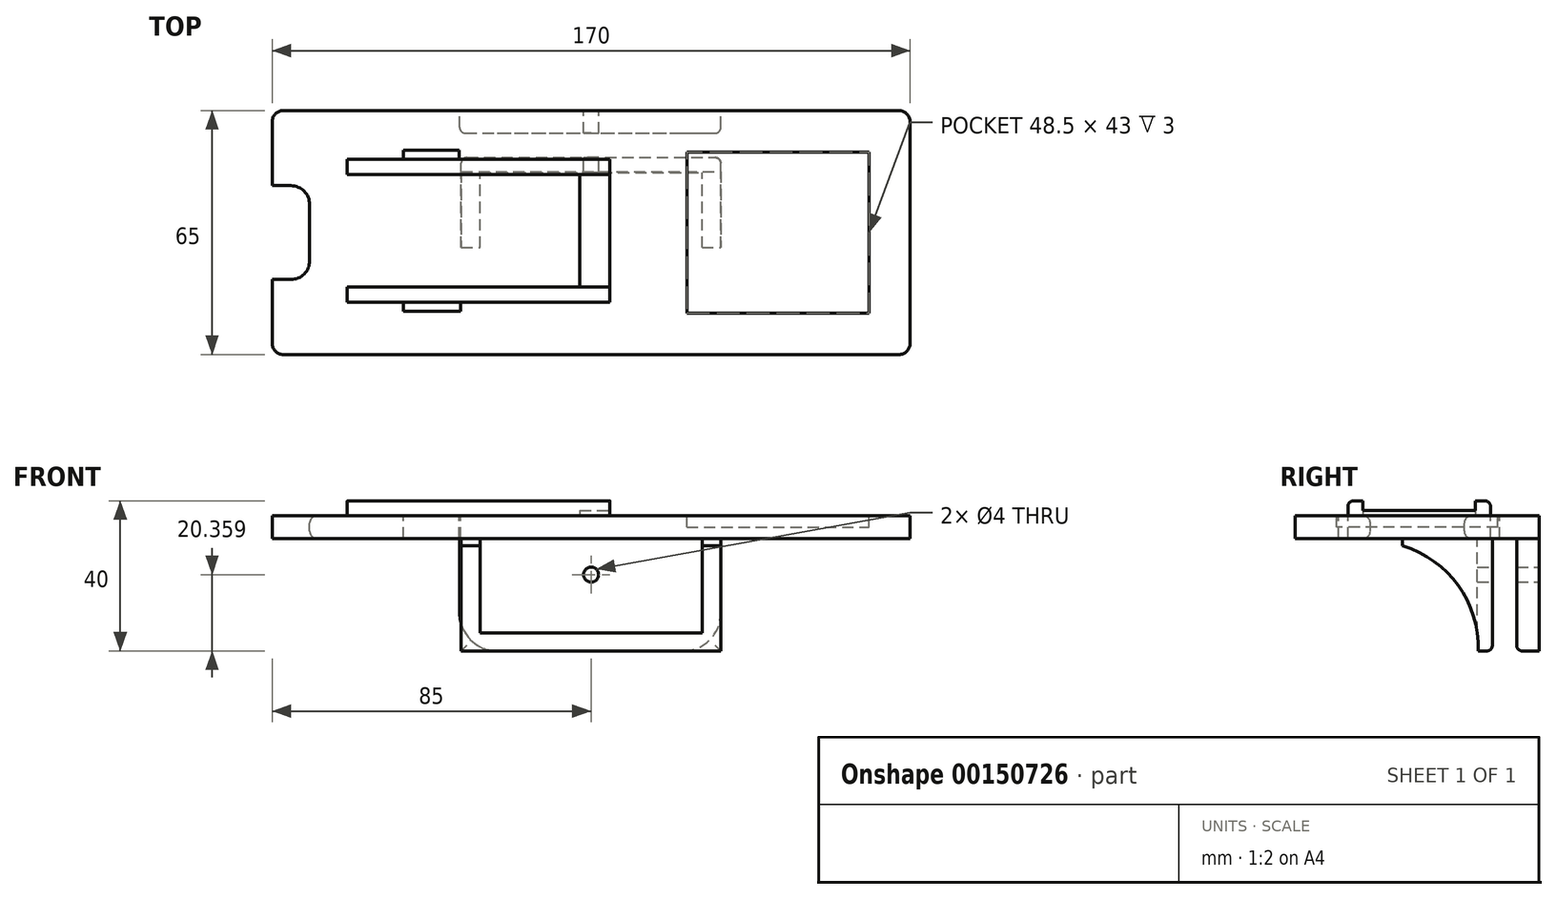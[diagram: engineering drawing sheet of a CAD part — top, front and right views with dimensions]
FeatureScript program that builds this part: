
annotation { "Feature Type Name" : "Feature", "Feature Type Description" : "" }
export const myFeature = defineFeature(function(context is Context, id is Id, definition is map)
    precondition{}
    {
        {
            var Q0;
            Q0=qCreatedBy(makeId("Front.planeOp"),FACE);
            var sketch = newSketch(context, id + "F0", { "sketchPlane" : qUnion([Q0])});
            skLineSegment(sketch, "E0.bottom", {"start": v(85, -3) * mm, "end": v(-85, -3) * mm});
            skLineSegment(sketch, "E0.top", {"start": v(85, 3) * mm, "end": v(-85, 3) * mm});
            skLineSegment(sketch, "E0.left", {"start": v(85, -3) * mm, "end": v(85, 3) * mm});
            skLineSegment(sketch, "E0.right", {"start": v(-85, -3) * mm, "end": v(-85, 3) * mm});
            skPoint(sketch, "E0.middle", {"position": v(0, 0) * mm});
            skSolve(sketch);
        }
        {
            var Q0;
            Q0=makeQuery(id+"F0.imprint","IMPRINT",FACE,{"disambiguationData":[TD([[makeQuery(id+"F0.imprint","IMPRINT",EDGE,{"derivedFrom":sQuery(id+"F0.wireOp",EDGE,"E0.bottom")}),-1.0]])]});
            extrude(context, id + "F1", {"entities" : qUnion([Q0]), "depth" : 65 * mm});
        }
        {
            var Q0;
            Q0=makeQuery(id+"F1.opExtrude","SWEPT_FACE",FACE,{"disambiguationData":[OSD([sQuery(id+"F0.wireOp",EDGE,"E0.top")])]});
            var sketch = newSketch(context, id + "F2", { "sketchPlane" : qUnion([Q0])});
            skLineSegment(sketch, "E1.bottom", {"start": v(25.5, -11) * mm, "end": v(74, -11) * mm});
            skLineSegment(sketch, "E1.top", {"start": v(25.5, -54) * mm, "end": v(74, -54) * mm});
            skLineSegment(sketch, "E1.left", {"start": v(25.5, -11) * mm, "end": v(25.5, -54) * mm});
            skLineSegment(sketch, "E1.right", {"start": v(74, -11) * mm, "end": v(74, -54) * mm});
            skSolve(sketch);
        }
        {
            var Q0;
            Q0=makeQuery(id+"F2.imprint","IMPRINT",FACE,{"disambiguationData":[TD([[makeQuery(id+"F2.imprint","IMPRINT",EDGE,{"derivedFrom":sQuery(id+"F2.wireOp",EDGE,"E1.bottom")}),-1.0]])]});
            extrude(context, id + "F3", {"entities" : qUnion([Q0]), "operationType" : NewBodyOperationType.REMOVE, "oppositeDirection" : true, "depth" : 3 * mm});
        }
        {
            var Q0;
            Q0=makeQuery(id+"F1.opExtrude","SWEPT_FACE",FACE,{"disambiguationData":[OSD([sQuery(id+"F0.wireOp",EDGE,"E0.top")])]});
            var sketch = newSketch(context, id + "F4", { "sketchPlane" : qUnion([Q0])});
            skLineSegment(sketch, "E2.bottom", {"start": v(-65, -13) * mm, "end": v(5, -13) * mm});
            skLineSegment(sketch, "E2.top", {"start": v(-65, -17) * mm, "end": v(5, -17) * mm});
            skLineSegment(sketch, "E2.left", {"start": v(-65, -13) * mm, "end": v(-65, -17) * mm});
            skLineSegment(sketch, "E2.right", {"start": v(5, -13) * mm, "end": v(5, -17) * mm});
            skLineSegment(sketch, "E3.bottom", {"start": v(-65, -47) * mm, "end": v(5, -47) * mm});
            skLineSegment(sketch, "E3.top", {"start": v(-65, -51) * mm, "end": v(5, -51) * mm});
            skLineSegment(sketch, "E3.left", {"start": v(-65, -47) * mm, "end": v(-65, -51) * mm});
            skLineSegment(sketch, "E3.right", {"start": v(5, -47) * mm, "end": v(5, -51) * mm});
            skSolve(sketch);
        }
        {
            var Q0;
            Q0=makeQuery(id+"F4.imprint","IMPRINT",FACE,{"disambiguationData":[TD([[makeQuery(id+"F4.imprint","IMPRINT",EDGE,{"derivedFrom":sQuery(id+"F4.wireOp",EDGE,"E2.bottom")}),-1.0]])]});
            var Q1;
            Q1=makeQuery(id+"F4.imprint","IMPRINT",FACE,{"disambiguationData":[TD([[makeQuery(id+"F4.imprint","IMPRINT",EDGE,{"derivedFrom":sQuery(id+"F4.wireOp",EDGE,"E3.bottom")}),-1.0]])]});
            extrude(context, id + "F5", {"entities" : qUnion([Q0, Q1]), "operationType" : NewBodyOperationType.ADD, "depth" : 4 * mm});
        }
        {
            var Q0;
            Q0=makeQuery(id+"F1.opExtrude","SWEPT_FACE",FACE,{"disambiguationData":[OSD([sQuery(id+"F0.wireOp",EDGE,"E0.bottom")])]});
            var sketch = newSketch(context, id + "F6", { "sketchPlane" : qUnion([Q0])});
            skLineSegment(sketch, "E4.bottom", {"start": v(-34.6, 16.5) * mm, "end": v(34.55, 16.5) * mm});
            skLineSegment(sketch, "E4.top", {"start": v(-34.6, 12.5) * mm, "end": v(34.55, 12.5) * mm});
            skLineSegment(sketch, "E4.left", {"start": v(-34.6, 16.5) * mm, "end": v(-34.6, 12.5) * mm});
            skLineSegment(sketch, "E4.right", {"start": v(34.55, 16.5) * mm, "end": v(34.55, 12.5) * mm});
            skLineSegment(sketch, "E5.bottom", {"start": v(-35, 6) * mm, "end": v(34.55, 6) * mm});
            skLineSegment(sketch, "E5.top", {"start": v(-35, 0) * mm, "end": v(34.55, 0) * mm});
            skLineSegment(sketch, "E5.left", {"start": v(-35, 6) * mm, "end": v(-35, 0) * mm});
            skLineSegment(sketch, "E5.right", {"start": v(34.55, 6) * mm, "end": v(34.55, 0) * mm});
            skSolve(sketch);
        }
        {
            var Q0;
            Q0=makeQuery(id+"F6.imprint","IMPRINT",FACE,{"disambiguationData":[TD([[makeQuery(id+"F6.imprint","IMPRINT",EDGE,{"derivedFrom":sQuery(id+"F6.wireOp",EDGE,"E4.bottom")}),-1.0]])]});
            var Q1;
            Q1=makeQuery(id+"F6.imprint","IMPRINT",FACE,{"disambiguationData":[TD([[makeQuery(id+"F6.imprint","IMPRINT",EDGE,{"derivedFrom":sQuery(id+"F6.wireOp",EDGE,"E5.bottom")}),-1.0]])]});
            extrude(context, id + "F7", {"entities" : qUnion([Q0, Q1]), "operationType" : NewBodyOperationType.ADD, "depth" : 30 * mm});
        }
        {
            var Q0;
            Q0=makeQuery(id+"F7.opExtrude","SWEPT_FACE",FACE,{"disambiguationData":[OSD([sQuery(id+"F6.wireOp",EDGE,"E4.bottom")])]});
            var sketch = newSketch(context, id + "F8", { "sketchPlane" : qUnion([Q0])});
            skLineSegment(sketch, "E6.bottom", {"start": v(-34.6, -33) * mm, "end": v(-29.6, -33) * mm});
            skLineSegment(sketch, "E6.top", {"start": v(-34.6, -3) * mm, "end": v(-29.6, -3) * mm});
            skLineSegment(sketch, "E6.left", {"start": v(-34.6, -33) * mm, "end": v(-34.6, -3) * mm});
            skLineSegment(sketch, "E6.right", {"start": v(-29.6, -33) * mm, "end": v(-29.6, -3) * mm});
            skLineSegment(sketch, "E7.bottom", {"start": v(34.55, -33) * mm, "end": v(29.55, -33) * mm});
            skLineSegment(sketch, "E7.top", {"start": v(34.55, -3) * mm, "end": v(29.55, -3) * mm});
            skLineSegment(sketch, "E7.left", {"start": v(34.55, -33) * mm, "end": v(34.55, -3) * mm});
            skLineSegment(sketch, "E7.right", {"start": v(29.55, -33) * mm, "end": v(29.55, -3) * mm});
            skSolve(sketch);
        }
        {
            var Q0;
            Q0=makeQuery(id+"F8.imprint","IMPRINT",FACE,{"disambiguationData":[TD([[makeQuery(id+"F8.imprint","IMPRINT",EDGE,{"derivedFrom":sQuery(id+"F8.wireOp",EDGE,"E6.bottom")}),1.0]])]});
            var Q1;
            Q1=makeQuery(id+"F8.imprint","IMPRINT",FACE,{"disambiguationData":[TD([[makeQuery(id+"F8.imprint","IMPRINT",EDGE,{"derivedFrom":sQuery(id+"F8.wireOp",EDGE,"E7.bottom")}),1.0]])]});
            extrude(context, id + "F9", {"entities" : qUnion([Q0, Q1]), "operationType" : NewBodyOperationType.ADD, "depth" : 20 * mm});
        }
        {
            var Q0;
            Q0=makeQuery(id+"F9.opExtrude","CAP_EDGE",EDGE,{"disambiguationData":[OSD([sQuery(id+"F8.wireOp",EDGE,"E6.bottom")])],"isStart":false});
            var Q1;
            Q1=makeQuery(id+"F9.opExtrude","CAP_EDGE",EDGE,{"disambiguationData":[OSD([sQuery(id+"F8.wireOp",EDGE,"E7.bottom")])],"isStart":false});
            chamfer(context, id + "F10", {"entities" : qUnion([Q0, Q1]), "chamferType" : ChamferType.TWO_OFFSETS, "width1" : 28 * mm, "oppositeDirection" : false, "width2" : 18 * mm, "tangentPropagation" : true});
        }
        {
            var Q0;
            Q0=makeQuery(id+"F1.opExtrude","SWEPT_FACE",FACE,{"disambiguationData":[OSD([sQuery(id+"F0.wireOp",EDGE,"E0.top")])]});
            var sketch = newSketch(context, id + "F11", { "sketchPlane" : qUnion([Q0])});
            skLineSegment(sketch, "E8.bottom", {"start": v(-35.2, -13) * mm, "end": v(-50, -13) * mm});
            skLineSegment(sketch, "E8.top", {"start": v(-35.2, -10.5) * mm, "end": v(-50, -10.5) * mm});
            skLineSegment(sketch, "E8.left", {"start": v(-35.2, -13) * mm, "end": v(-35.2, -10.5) * mm});
            skLineSegment(sketch, "E8.right", {"start": v(-50, -13) * mm, "end": v(-50, -10.5) * mm});
            skLineSegment(sketch, "E9.bottom", {"start": v(-34.83, -51) * mm, "end": v(-50, -51) * mm});
            skLineSegment(sketch, "E9.top", {"start": v(-34.83, -53.5) * mm, "end": v(-50, -53.5) * mm});
            skLineSegment(sketch, "E9.left", {"start": v(-34.83, -51) * mm, "end": v(-34.83, -53.5) * mm});
            skLineSegment(sketch, "E9.right", {"start": v(-50, -51) * mm, "end": v(-50, -53.5) * mm});
            skSolve(sketch);
        }
        {
            var Q0;
            Q0 = qSketchRegion(id + "F11", true);
            extrude(context, id + "F12", {"entities" : qUnion([Q0]), "operationType" : NewBodyOperationType.REMOVE, "endBound" : BoundingType.THROUGH_ALL, "oppositeDirection" : true, "depth" : 25 * mm});
        }
        {
            var Q0;
            Q0=makeQuery(id+"F7.opExtrude","CAP_EDGE",EDGE,{"disambiguationData":[OSD([sQuery(id+"F6.wireOp",EDGE,"E5.left")])],"isStart":false});
            var Q1;
            Q1=makeQuery(id+"F7.opExtrude","CAP_EDGE",EDGE,{"disambiguationData":[OSD([sQuery(id+"F6.wireOp",EDGE,"E5.right")])],"isStart":false});
            fillet(context, id + "F13", {"entities" : qUnion([Q0, Q1]), "radius" : 10 * mm, "tangentPropagation" : true, "allowEdgeOverflow" : false});
        }
        {
            var Q0;
            Q0=makeQuery(id+"F7.opExtrude","SWEPT_EDGE",EDGE,{"disambiguationData":[OSD([sQuery(id+"F6.wireOp",EDGE,"E4.top"),sQuery(id+"F6.wireOp",EDGE,"E4.left")])]});
            var Q1;
            Q1=makeQuery(id+"F7.opExtrude","SWEPT_EDGE",EDGE,{"disambiguationData":[OSD([sQuery(id+"F6.wireOp",EDGE,"E4.top"),sQuery(id+"F6.wireOp",EDGE,"E4.right")])]});
            var Q2;
            Q2=makeQuery(id+"F7.opExtrude","CAP_EDGE",EDGE,{"disambiguationData":[OSD([sQuery(id+"F6.wireOp",EDGE,"E4.top")])],"isStart":false});
            fillet(context, id + "F14", {"entities" : qUnion([Q0, Q1, Q2]), "radius" : 1.5 * mm, "tangentPropagation" : true, "allowEdgeOverflow" : false});
        }
        {
            var Q0;
            Q0=makeQuery(id+"F7.opExtrude","SWEPT_EDGE",EDGE,{"disambiguationData":[OSD([sQuery(id+"F6.wireOp",EDGE,"E5.bottom"),sQuery(id+"F6.wireOp",EDGE,"E5.right")])]});
            var Q1;
            Q1=makeQuery(id+"F13.opFillet","BLEND_EDGE",EDGE,{"blendedFrom":[makeQuery(id+"F7.opExtrude","CAP_EDGE",EDGE,{"disambiguationData":[OSD([sQuery(id+"F6.wireOp",EDGE,"E5.right")])],"isStart":false}),makeQuery(id+"F7.opExtrude","SWEPT_FACE",FACE,{"disambiguationData":[OSD([sQuery(id+"F6.wireOp",EDGE,"E5.bottom")])]})],"blendedInto":[makeQuery(id+"F7.opExtrude","SWEPT_FACE",FACE,{"disambiguationData":[OSD([sQuery(id+"F6.wireOp",EDGE,"E5.bottom")])]})]});
            var Q2;
            Q2=makeQuery(id+"F7.opExtrude","CAP_EDGE",EDGE,{"disambiguationData":[OSD([sQuery(id+"F6.wireOp",EDGE,"E5.bottom")])],"isStart":false});
            var Q3;
            Q3=makeQuery(id+"F13.opFillet","BLEND_EDGE",EDGE,{"blendedFrom":[makeQuery(id+"F7.opExtrude","CAP_EDGE",EDGE,{"disambiguationData":[OSD([sQuery(id+"F6.wireOp",EDGE,"E5.left")])],"isStart":false}),makeQuery(id+"F7.opExtrude","SWEPT_FACE",FACE,{"disambiguationData":[OSD([sQuery(id+"F6.wireOp",EDGE,"E5.bottom")])]})],"blendedInto":[makeQuery(id+"F7.opExtrude","SWEPT_FACE",FACE,{"disambiguationData":[OSD([sQuery(id+"F6.wireOp",EDGE,"E5.bottom")])]})]});
            var Q4;
            Q4=makeQuery(id+"F7.opExtrude","SWEPT_EDGE",EDGE,{"disambiguationData":[OSD([sQuery(id+"F6.wireOp",EDGE,"E5.bottom"),sQuery(id+"F6.wireOp",EDGE,"E5.left")])]});
            fillet(context, id + "F15", {"entities" : qUnion([Q0, Q1, Q2, Q3, Q4]), "radius" : 1.5 * mm, "tangentPropagation" : true, "allowEdgeOverflow" : false});
        }
        {
            var Q0;
            Q0=makeQuery(id+"F1.opExtrude","CAP_EDGE",EDGE,{"disambiguationData":[OSD([sQuery(id+"F0.wireOp",EDGE,"E0.right")])],"isStart":false});
            var Q1;
            Q1=makeQuery(id+"F1.opExtrude","CAP_EDGE",EDGE,{"disambiguationData":[OSD([sQuery(id+"F0.wireOp",EDGE,"E0.right")])],"isStart":true});
            var Q2;
            Q2=makeQuery(id+"F1.opExtrude","CAP_EDGE",EDGE,{"disambiguationData":[OSD([sQuery(id+"F0.wireOp",EDGE,"E0.left")])],"isStart":true});
            var Q3;
            Q3=makeQuery(id+"F1.opExtrude","CAP_EDGE",EDGE,{"disambiguationData":[OSD([sQuery(id+"F0.wireOp",EDGE,"E0.left")])],"isStart":false});
            fillet(context, id + "F16", {"entities" : qUnion([Q0, Q1, Q2, Q3]), "radius" : 3 * mm, "tangentPropagation" : true, "allowEdgeOverflow" : false});
        }
        {
            var Q0;
            Q0=makeQuery(id+"F9.boolean.opBoolean","MERGE",FACE,{"derivedFrom":[makeQuery(id+"F7.opExtrude","SWEPT_FACE",FACE,{"disambiguationData":[OSD([sQuery(id+"F6.wireOp",EDGE,"E4.right")])]}),makeQuery(id+"F9.opExtrude","SWEPT_FACE",FACE,{"disambiguationData":[OSD([sQuery(id+"F8.wireOp",EDGE,"E7.left")])]})]});
            var sketch = newSketch(context, id + "F17", { "sketchPlane" : qUnion([Q0])});
            skArc(sketch, "E10", {"start": v(-16.25, -33) * mm, "mid": v(-21.57, -15.53) * mm, "end": v(-36.5, -5) * mm});
            skSolve(sketch);
        }
        {
            var Q0;
            {var subQ0=sQuery(id+"F17.wireOp",EDGE,"E10");Q0=makeQuery(id+"F17.imprint","IMPRINT",FACE,{"disambiguationData":[TD([[makeQuery(id+"F17.imprint","IMPRINT",EDGE,{"derivedFrom":subQ0}),1.0]])]});}
            extrude(context, id + "F18", {"entities" : qUnion([Q0]), "operationType" : NewBodyOperationType.REMOVE, "endBound" : BoundingType.THROUGH_ALL, "oppositeDirection" : true, "depth" : 25 * mm});
        }
        {
            var Q0;
            Q0=makeQuery(id+"F7.boolean.opBoolean","MERGE",FACE,{"derivedFrom":[makeQuery(id+"F1.opExtrude","CAP_FACE",FACE,{"disambiguationData":[OSD([sQuery(id+"F0.wireOp",EDGE,"E0.bottom"),sQuery(id+"F0.wireOp",EDGE,"E0.top"),sQuery(id+"F0.wireOp",EDGE,"E0.left"),sQuery(id+"F0.wireOp",EDGE,"E0.right")])],"isStart":true}),makeQuery(id+"F7.opExtrude","SWEPT_FACE",FACE,{"disambiguationData":[OSD([sQuery(id+"F6.wireOp",EDGE,"E5.top")])]})]});
            var sketch = newSketch(context, id + "F19", { "sketchPlane" : qUnion([Q0])});
            skPoint(sketch, "E11", {"position": v(0, -12.64) * mm});
            skSolve(sketch);
        }
        {
            var Q0;
            Q0=sQuery(id+"F19.wireOp",VERTEX,"E11");
            var Q1;
            Q1=makeQuery(id+"F1.opExtrude","SWEPT_BODY",BODY,{"disambiguationData":[OSD([sQuery(id+"F0.wireOp",EDGE,"E0.bottom"),sQuery(id+"F0.wireOp",EDGE,"E0.top"),sQuery(id+"F0.wireOp",EDGE,"E0.left"),sQuery(id+"F0.wireOp",EDGE,"E0.right")])]});
            hole(context, id + "F20", {"style" : HoleStyle.SIMPLE, "endStyle" : HoleEndStyle.THROUGH, "holeDiameter" : 4 * mm, "locations" : qUnion([Q0]), "scope" : qUnion([Q1]), "isTappedThrough" : true});
        }
        {
            var Q0;
            Q0=makeQuery(id+"F1.opExtrude","SWEPT_FACE",FACE,{"disambiguationData":[OSD([sQuery(id+"F0.wireOp",EDGE,"E0.top")])]});
            var sketch = newSketch(context, id + "F21", { "sketchPlane" : qUnion([Q0])});
            skLineSegment(sketch, "E12.bottom", {"start": v(-85, -20) * mm, "end": v(-75, -20) * mm});
            skLineSegment(sketch, "E12.top", {"start": v(-85, -45) * mm, "end": v(-75, -45) * mm});
            skLineSegment(sketch, "E12.left", {"start": v(-85, -20) * mm, "end": v(-85, -45) * mm});
            skLineSegment(sketch, "E12.right", {"start": v(-75, -20) * mm, "end": v(-75, -45) * mm});
            skSolve(sketch);
        }
        {
            var Q0;
            Q0=makeQuery(id+"F21.imprint","IMPRINT",FACE,{"disambiguationData":[TD([[makeQuery(id+"F21.imprint","IMPRINT",EDGE,{"derivedFrom":sQuery(id+"F21.wireOp",EDGE,"E12.bottom")}),-1.0]])]});
            extrude(context, id + "F22", {"entities" : qUnion([Q0]), "operationType" : NewBodyOperationType.REMOVE, "oppositeDirection" : true, "depth" : 25 * mm});
        }
        {
            var Q0;
            Q0=makeQuery(id+"F22.boolean.opBoolean","COPY",EDGE,{"derivedFrom":makeQuery(id+"F22.opExtrude","SWEPT_EDGE",EDGE,{"disambiguationData":[OSD([sQuery(id+"F21.wireOp",EDGE,"E12.bottom"),sQuery(id+"F21.wireOp",EDGE,"E12.right")])]})});
            var Q1;
            Q1=makeQuery(id+"F22.boolean.opBoolean","COPY",EDGE,{"derivedFrom":makeQuery(id+"F22.opExtrude","SWEPT_EDGE",EDGE,{"disambiguationData":[OSD([sQuery(id+"F21.wireOp",EDGE,"E12.top"),sQuery(id+"F21.wireOp",EDGE,"E12.right")])]})});
            fillet(context, id + "F23", {"entities" : qUnion([Q0, Q1]), "radius" : 5 * mm, "tangentPropagation" : true, "allowEdgeOverflow" : false});
        }
        {
            var Q0;
            Q0=makeQuery(id+"F22.boolean.opBoolean","COPY",EDGE,{"derivedFrom":makeQuery(id+"F22.opExtrude","CAP_EDGE",EDGE,{"disambiguationData":[OSD([sQuery(id+"F21.wireOp",EDGE,"E12.right")])],"isStart":true})});
            var Q1;
            Q1=makeQuery(id+"F23.opFillet","BLEND_EDGE",EDGE,{"blendedFrom":[makeQuery(id+"F22.boolean.opBoolean","COPY",EDGE,{"derivedFrom":makeQuery(id+"F22.opExtrude","SWEPT_EDGE",EDGE,{"disambiguationData":[OSD([sQuery(id+"F21.wireOp",EDGE,"E12.bottom"),sQuery(id+"F21.wireOp",EDGE,"E12.right")])]})}),makeQuery(id+"F1.opExtrude","SWEPT_FACE",FACE,{"disambiguationData":[OSD([sQuery(id+"F0.wireOp",EDGE,"E0.top")])]})],"blendedInto":[makeQuery(id+"F1.opExtrude","SWEPT_FACE",FACE,{"disambiguationData":[OSD([sQuery(id+"F0.wireOp",EDGE,"E0.top")])]})]});
            var Q2;
            Q2=makeQuery(id+"F22.boolean.opBoolean","COPY",EDGE,{"derivedFrom":makeQuery(id+"F22.opExtrude","CAP_EDGE",EDGE,{"disambiguationData":[OSD([sQuery(id+"F21.wireOp",EDGE,"E12.bottom")])],"isStart":true})});
            var Q3;
            Q3=makeQuery(id+"F23.opFillet","BLEND_EDGE",EDGE,{"blendedFrom":[makeQuery(id+"F22.boolean.opBoolean","COPY",EDGE,{"derivedFrom":makeQuery(id+"F22.opExtrude","SWEPT_EDGE",EDGE,{"disambiguationData":[OSD([sQuery(id+"F21.wireOp",EDGE,"E12.top"),sQuery(id+"F21.wireOp",EDGE,"E12.right")])]})}),makeQuery(id+"F1.opExtrude","SWEPT_FACE",FACE,{"disambiguationData":[OSD([sQuery(id+"F0.wireOp",EDGE,"E0.top")])]})],"blendedInto":[makeQuery(id+"F1.opExtrude","SWEPT_FACE",FACE,{"disambiguationData":[OSD([sQuery(id+"F0.wireOp",EDGE,"E0.top")])]})]});
            var Q4;
            Q4=makeQuery(id+"F22.boolean.opBoolean","COPY",EDGE,{"derivedFrom":makeQuery(id+"F22.opExtrude","CAP_EDGE",EDGE,{"disambiguationData":[OSD([sQuery(id+"F21.wireOp",EDGE,"E12.top")])],"isStart":true})});
            fillet(context, id + "F24", {"entities" : qUnion([Q0, Q1, Q2, Q3, Q4]), "radius" : 2 * mm, "tangentPropagation" : true, "allowEdgeOverflow" : false});
        }
        {
            var Q0;
            Q0=makeQuery(id+"F22.boolean.opBoolean","INTERSECT",EDGE,{"derivedFrom":[makeQuery(id+"F1.opExtrude","SWEPT_FACE",FACE,{"disambiguationData":[OSD([sQuery(id+"F0.wireOp",EDGE,"E0.bottom")])]}),makeQuery(id+"F22.opExtrude","SWEPT_FACE",FACE,{"disambiguationData":[OSD([sQuery(id+"F21.wireOp",EDGE,"E12.top")])]})]});
            var Q1;
            Q1=makeQuery(id+"F23.opFillet","BLEND_EDGE",EDGE,{"blendedFrom":[makeQuery(id+"F22.boolean.opBoolean","COPY",EDGE,{"derivedFrom":makeQuery(id+"F22.opExtrude","SWEPT_EDGE",EDGE,{"disambiguationData":[OSD([sQuery(id+"F21.wireOp",EDGE,"E12.top"),sQuery(id+"F21.wireOp",EDGE,"E12.right")])]})}),makeQuery(id+"F1.opExtrude","SWEPT_FACE",FACE,{"disambiguationData":[OSD([sQuery(id+"F0.wireOp",EDGE,"E0.bottom")])]})],"blendedInto":[makeQuery(id+"F1.opExtrude","SWEPT_FACE",FACE,{"disambiguationData":[OSD([sQuery(id+"F0.wireOp",EDGE,"E0.bottom")])]})]});
            var Q2;
            Q2=makeQuery(id+"F22.boolean.opBoolean","INTERSECT",EDGE,{"derivedFrom":[makeQuery(id+"F1.opExtrude","SWEPT_FACE",FACE,{"disambiguationData":[OSD([sQuery(id+"F0.wireOp",EDGE,"E0.bottom")])]}),makeQuery(id+"F22.opExtrude","SWEPT_FACE",FACE,{"disambiguationData":[OSD([sQuery(id+"F21.wireOp",EDGE,"E12.right")])]})]});
            var Q3;
            Q3=makeQuery(id+"F23.opFillet","BLEND_EDGE",EDGE,{"blendedFrom":[makeQuery(id+"F22.boolean.opBoolean","COPY",EDGE,{"derivedFrom":makeQuery(id+"F22.opExtrude","SWEPT_EDGE",EDGE,{"disambiguationData":[OSD([sQuery(id+"F21.wireOp",EDGE,"E12.bottom"),sQuery(id+"F21.wireOp",EDGE,"E12.right")])]})}),makeQuery(id+"F1.opExtrude","SWEPT_FACE",FACE,{"disambiguationData":[OSD([sQuery(id+"F0.wireOp",EDGE,"E0.bottom")])]})],"blendedInto":[makeQuery(id+"F1.opExtrude","SWEPT_FACE",FACE,{"disambiguationData":[OSD([sQuery(id+"F0.wireOp",EDGE,"E0.bottom")])]})]});
            var Q4;
            Q4=makeQuery(id+"F22.boolean.opBoolean","INTERSECT",EDGE,{"derivedFrom":[makeQuery(id+"F1.opExtrude","SWEPT_FACE",FACE,{"disambiguationData":[OSD([sQuery(id+"F0.wireOp",EDGE,"E0.bottom")])]}),makeQuery(id+"F22.opExtrude","SWEPT_FACE",FACE,{"disambiguationData":[OSD([sQuery(id+"F21.wireOp",EDGE,"E12.bottom")])]})]});
            fillet(context, id + "F25", {"entities" : qUnion([Q0, Q1, Q2, Q3, Q4]), "radius" : 2 * mm, "tangentPropagation" : true, "allowEdgeOverflow" : false});
        }
        {
            var Q0;
            Q0=makeQuery(id+"F5.opExtrude","CAP_EDGE",EDGE,{"disambiguationData":[OSD([sQuery(id+"F4.wireOp",EDGE,"E2.bottom")])],"isStart":false});
            var Q1;
            Q1=makeQuery(id+"F5.opExtrude","CAP_EDGE",EDGE,{"disambiguationData":[OSD([sQuery(id+"F4.wireOp",EDGE,"E3.top")])],"isStart":false});
            fillet(context, id + "F26", {"entities" : qUnion([Q0, Q1]), "radius" : 1.5 * mm, "tangentPropagation" : true, "allowEdgeOverflow" : false});
        }
        {
            var Q0;
            Q0=makeQuery(id+"F1.opExtrude","SWEPT_FACE",FACE,{"disambiguationData":[OSD([sQuery(id+"F0.wireOp",EDGE,"E0.top")])]});
            var sketch = newSketch(context, id + "F27", { "sketchPlane" : qUnion([Q0])});
            skLineSegment(sketch, "E13.bottom", {"start": v(5, -17) * mm, "end": v(-3, -17) * mm});
            skLineSegment(sketch, "E13.top", {"start": v(5, -47) * mm, "end": v(-3, -47) * mm});
            skLineSegment(sketch, "E13.left", {"start": v(5, -17) * mm, "end": v(5, -47) * mm});
            skLineSegment(sketch, "E13.right", {"start": v(-3, -17) * mm, "end": v(-3, -47) * mm});
            skSolve(sketch);
        }
        {
            var Q0;
            Q0=makeQuery(id+"F27.imprint","IMPRINT",FACE,{"disambiguationData":[TD([[makeQuery(id+"F27.imprint","IMPRINT",EDGE,{"derivedFrom":sQuery(id+"F27.wireOp",EDGE,"E13.bottom")}),-1.0]])]});
            extrude(context, id + "F28", {"entities" : qUnion([Q0]), "operationType" : NewBodyOperationType.ADD, "depth" : 1.5 * mm});
        }
    });
